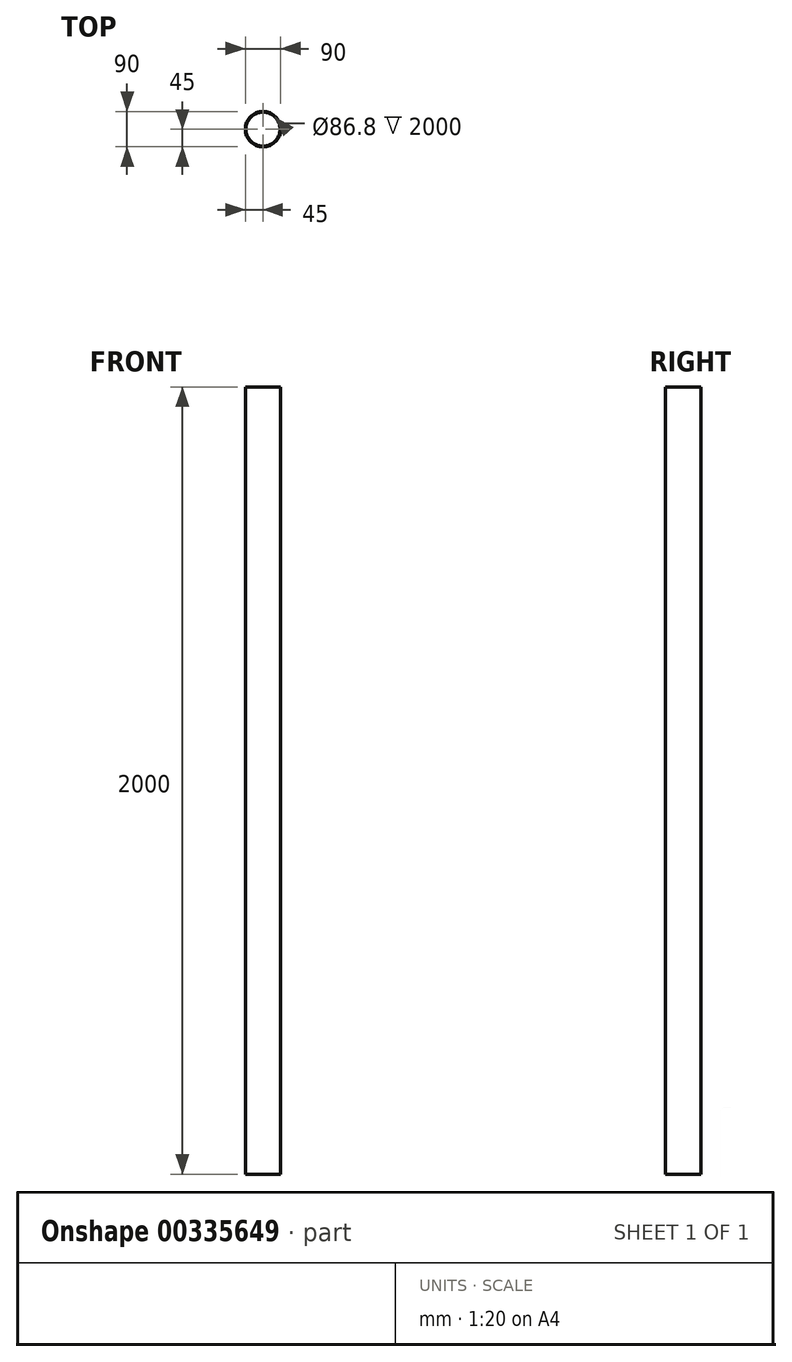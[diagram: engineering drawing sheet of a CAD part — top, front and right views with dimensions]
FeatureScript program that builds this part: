
annotation { "Feature Type Name" : "Feature", "Feature Type Description" : "" }
export const myFeature = defineFeature(function(context is Context, id is Id, definition is map)
    precondition{}
    {
        {
            var Q0;
            Q0=qCreatedBy(makeId("Top.planeOp"),FACE);
            var sketch = newSketch(context, id + "F0", { "sketchPlane" : qUnion([Q0])});
            skCircle(sketch, "E0", {"center": v(0, 0) * mm, "radius": 45 * mm});
            skCircle(sketch, "E1", {"center": v(0, 0) * mm, "radius": 43.4 * mm});
            skSolve(sketch);
        }
        {
            var Q0;
            Q0=makeQuery(id+"F0.imprint","IMPRINT",FACE,{"disambiguationData":[TD([[makeQuery(id+"F0.imprint","IMPRINT",EDGE,{"derivedFrom":sQuery(id+"F0.wireOp",EDGE,"E0")}),1.0]])]});
            extrude(context, id + "F1", {"entities" : qUnion([Q0]), "depth" : 2000 * mm});
        }
    });
